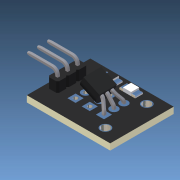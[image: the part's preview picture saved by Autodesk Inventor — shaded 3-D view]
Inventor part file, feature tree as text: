
AUTODESK INVENTOR PART (.ipt)
format: ipt  version: 2020.3 (Build 243373000, 373)  size: 1,203,712 bytes
history: native  units: mm
features: other x26, sketch x17, extrude x10, plane x6, fillet x4, pattern_linear x3, chamfer x3, hole x2, mirror x2, surface_op x2, revolve x1, loft x1
ambient origin geometry x8: Origin, YZ Plane, XZ Plane, XY Plane, X Axis, Y Axis, Z Axis, Center Point
bodies: Body1 (feature_tree), Body2 (feature_tree), Body3 (feature_tree)
feature tree (77):
  other  "Volume4"
  extrude  "Extrusion4"  Depth=20.55mm
  hole  "Bohrung1"  [1 undecoded]
  mirror  "Spiegeln1"
  other  "Trennen5"
  other  "Trennen6"
  extrude  "Extrusion5"  Depth=6.5mm
  extrude  "Extrusion6"  Depth=2.0mm
  fillet  "Rundung1"  Radius=4.0mm
  fillet  "Rundung2"  Radius=0.87mm
  plane  "Arbeitsebene1"
  plane  "Arbeitsebene2"
  other  "Trennen1"
  other  "Trennen2"
  other  "Trennen3"
  other  "Trennen4"
  pattern_linear  "Rechteckige Anordnung1"  Count1=2 Spacing1=5.0mm
  extrude  "Extrusion7"  Depth=1.0mm
  extrude  "Extrusion8"  TaperAngle=0.0deg  [1 undecoded]
  revolve  "Umdrehung1"
  chamfer  "Fase1"  Distance=0.35mm Angle=45.0deg
  chamfer  "Fase2"  Distance=30.0mm
  pattern_linear  "Rechteckige Anordnung2"  Spacing1=1.0mm  [1 undecoded]
  pattern_linear  "Rechteckige Anordnung3"  Count1=3  [1 undecoded]
  fillet  "Rundung3"  Radius=2.46mm
  plane  "Arbeitsebene3"
  other  "Biegungsteil2"
  plane  "Arbeitsebene4"
  extrude  "Extrusion9"  Depth=10.0mm
  sketch  "Skizze14"  dims[d35=2.46mm d36=0.0mm d37=0.35mm d38=2.0mm d39=45.0deg d40=30.0mm d42=2.46mm]
  sketch  "Skizze15"  dims[d43=0.63mm]
  extrude  "Extrusion10"  Depth=10.0mm TaperAngle=90.0deg
  loft  "Erhebung1"
  mirror  "Spiegeln2"
  extrude  "Extrusion11"  Depth=10.0mm
  chamfer  "Fase3"  Distance=3.6mm
  fillet  "Rundung4"  Radius=0.872665mm
  hole  "Bohrung2"  [1 undecoded]
  sketch  "Skizze20"  dims[d59=0.890955mm]
  other  "Trennen7"
  other  "Trennen8"
  other  "Trennen9"
  other  "Trennen10"
  other  "Trennen11"
  other  "Trennen12"
  other  "Trennen13"
  other  "Trennen14"
  other  "Trennen15"
  sketch  "Skizze21"  dims[d60=1.22173mm d61=1.0mm d62=30.0mm d64=2.46mm d65=0.2mm d66=1.25mm d67=90.0deg d68=3.25mm d69=4.6mm d70=3.6mm d71=0.872665mm d72=6.0mm d73=4.3mm d74=0.0mm d75=0.2mm d76=10.0mm d77=0.0mm d78=0.63mm d79=6.9mm d80=2.46mm d81=1.25mm d82=10.0mm d83=0.0mm d84=10.0mm d85=90.0deg d86=10.0mm d87=90.0deg d88=3.05mm d89=0.0mm d90=0.05mm d91=2.0mm d92=45.0deg d93=0.2mm d94=1.0mm d95=6.981317mm d96=1.85mm d97=1.1mm d98=4.363323mm d123=0.685mm d124=0.685mm d125=2.46mm d126=3.5mm d127=3.5mm d128=1.0mm d129=6.0mm d130=4.0mm d131=2.0mm d132=90.0deg d133=8.0mm d134=20.594885mm d135=2.0mm d136=2.0mm]
  other  "Trennen16"
  other  "Trennen17"
  other  "Trennen18"
  other  "Trennen19"
  other  "Trennen20"
  other  "Trennen21"
  other  "Trennen22"
  plane  "Arbeitsebene5"
  other  "Biegungsteil3"
  plane  "Arbeitsebene6"
  other  "Biegungsteil4"
  sketch  "Skizze4"  dims[d6=15.65mm d7=20.55mm]
  sketch  "Skizze5"  dims[d8=1.55mm d9=0.0mm d10=10.2mm]
  sketch  "Skizze6"  dims[d11=3.9mm]
  sketch  "Skizze7"  dims[d12=2.0mm d13=50.0mm d14=4.0mm d15=2.0mm d16=90.0deg d17=8.0mm d18=20.594885mm d19=6.5mm]
  sketch  "Skizze8"  dims[d20=1.0mm d21=2.0mm d22=4.0mm d23=0.87mm d24=0.0mm]
  sketch  "Skizze9"  dims[d25=2.0mm]
  sketch  "Skizze10"  dims[d26=0.42mm d27=0.0mm]
  sketch  "Skizze11"  dims[d28=0.3mm]
  sketch  "Skizze12"  dims[d29=0.1mm d30=20.0mm d32=5.0mm]
  sketch  "Skizze13"  dims[d33=2.46mm d34=1.0mm]
  surface_op  "Surface1"
  surface_op  "Surface2"
  sketch  "Skizze16"  dims[d44=8.2mm d45=5.51mm d46=0.0mm d47=0.0mm]
  sketch  "Skizze17"  dims[d52=0.05mm d53=2.0mm d54=45.0deg]
  sketch  "Skizze19"  dims[d58=90.0deg]
  extrude  "Extrusionsfläche1"  Depth=10.0mm TaperAngle=0.0deg
  extrude  "Extrusionsfläche2"  Depth=10.0mm
note: 5 required parameter values undecoded (feature->parameter linkage not recoverable at this tier; creation-order binding heuristic only, values carry confidence <= 0.55)
